# Revit family: RN 85142 Optiflex-Profix-Té
name_source: partatom
category: Rohrformteile
units: mm (PartAtom-declared; Revit-internal decimal feet)

## family parameters
Arbeitsebenenbasiert = Nein
Beim Laden mit Abzugskörper schneiden = Nein
Bemaßung runder Anschluss = Durchmesser verwenden
Gemeinsam genutzt = Nein
Immer vertikal = Ja
Teiletyp = T-Stück

## types (11) — shared parameters
1.010.00.2 Blattnummer der Richtlinie = 29
1.010.00.3 Ausgabedatum (Monat) der Richtlinie = 201308
1.010.00.4 Herstellername = R. Nussbaum AG
1.010.00.5 Revisionsdatum der Datei = 20190521
1.010.00.6 Webadresse des Herstellers = http://www.nussbaum.ch
1.100.00.4 Produktbezeichnung = Versorgung
1.110.00.2 Index = 5
1.110.00.4 Produktbezeichnung = Optiflex
1.960/3L.00.8 Link (URL) = https://www.nussbaum.ch
29.700.00.4 Produktname = Optiflex-Profix-T-Stück
29.700.00.5 Produktkennung = 2
29.700.00.6 Querschnittsform = 1
29.700.00.7 Nennweitensystem = DN
29.700.00.8 Nenndrucksystem = PN
29.710.02.4 Nenndruck = 10
29.710.02.5 max. zul. Überdruck [hPa] = 1000
29.710.02.7 max. zul. Dauer-Betriebsdruck [hPa] = 1000
29.710.02.9 max. zul. Dauer-Betriebstemperatur [°C] = 70
Connector Visibility = Nein
EnclosingSpace Visibility = Nein
Hersteller = R. Nussbaum AG
R. Nussbaum AG 85142.25 de Visibility = Nein
R. Nussbaum AG 85142.29 de Visibility = Nein
R. Nussbaum AG 85142.30 de Visibility = Nein
URL = https://www.nussbaum.ch

## per-type parameters (varying)
- DN=20x15x20: 1.800.00.3 TGA-Nummer=01900500000000000000000000000000000000000000000056000000000000000008; 1.800.00.4 Kommentarfeld=85142.28, Optiflex-Profix-T-Stück, DN=20x15x20, L=128; 1.810.00.3 Hersteller-Bestellnummer=85142.28; 1.810.00.4 DATANORM-Nummer=85142.28; 1.810.00.5 StLB-Nummer=331.633; 1.810.00.6 GTIN-Nummer=7612945698001; 29.710.02.10 Formstück-Gewicht [kg]=0.363; 29.710.02.3 Benennung=Optiflex-Profix-T-Stück, DN=20x15x20, L=128; CONNECTOR0_DIAMETER_dY_0r=20 mm; CONNECTOR0_dY_00=22 mm; CONNECTOR0_dY_01=64 mm; CONNECTOR0_ref_dY=22 mm; CONNECTOR1_DIAMETER_dY_0r=20 mm; CONNECTOR1_dY_00=64 mm; CONNECTOR1_dY_01=22 mm; CONNECTOR1_ref_dY=22 mm; CONNECTOR2_DIAMETER_dX_0r=12 mm  [stored 0.0393701 ft]; CONNECTOR2_dX_00=56 mm; CONNECTOR2_dX_01=22 mm; CONNECTOR2_ref_dX=22 mm; Modell=85142.28; R. Nussbaum AG 85142.21 de Visibility=Nein; R. Nussbaum AG 85142.22 de Visibility=Nein; R. Nussbaum AG 85142.23 de Visibility=Nein; R. Nussbaum AG 85142.24 de Visibility=Nein; R. Nussbaum AG 85142.26 de Visibility=Nein; R. Nussbaum AG 85142.27 de Visibility=Nein; R. Nussbaum AG 85142.28 de Visibility=Ja; R. Nussbaum AG 85142.31 de Visibility=Nein; Typenkommentare=Optiflex-Profix-Té  DN=20x15x20
- DN=25: 1.800.00.3 TGA-Nummer=01900500000000000000000000000000000000000000000056000000000000000010; 1.800.00.4 Kommentarfeld=85142.31, Optiflex-Profix-T-Stück, DN=25, L=128; 1.810.00.3 Hersteller-Bestellnummer=85142.31; 1.810.00.4 DATANORM-Nummer=85142.31; 1.810.00.5 StLB-Nummer=331.633; 1.810.00.6 GTIN-Nummer=7612945698032; 29.710.02.10 Formstück-Gewicht [kg]=0.43; 29.710.02.3 Benennung=Optiflex-Profix-T-Stück, DN=25, L=128; CONNECTOR0_DIAMETER_dY_0r=20 mm; CONNECTOR0_dY_00=22 mm; CONNECTOR0_dY_01=64 mm; CONNECTOR0_ref_dY=22 mm; CONNECTOR1_DIAMETER_dY_0r=20 mm; CONNECTOR1_dY_00=64 mm; CONNECTOR1_dY_01=22 mm; CONNECTOR1_ref_dY=22 mm; CONNECTOR2_DIAMETER_dX_0r=20 mm; CONNECTOR2_dX_00=64 mm; CONNECTOR2_dX_01=22 mm; CONNECTOR2_ref_dX=22 mm; Modell=85142.31; R. Nussbaum AG 85142.21 de Visibility=Nein; R. Nussbaum AG 85142.22 de Visibility=Nein; R. Nussbaum AG 85142.23 de Visibility=Nein; R. Nussbaum AG 85142.24 de Visibility=Nein; R. Nussbaum AG 85142.26 de Visibility=Nein; R. Nussbaum AG 85142.27 de Visibility=Nein; R. Nussbaum AG 85142.28 de Visibility=Nein; R. Nussbaum AG 85142.31 de Visibility=Ja; Typenkommentare=Optiflex-Profix-Té  DN=25
- DN=20x15x15: 1.800.00.3 TGA-Nummer=01900500000000000000000000000000000000000000000056000000000000000007; 1.800.00.4 Kommentarfeld=85142.27, Optiflex-Profix-T-Stück, DN=20x15x15, L=120; 1.810.00.3 Hersteller-Bestellnummer=85142.27; 1.810.00.4 DATANORM-Nummer=85142.27; 1.810.00.5 StLB-Nummer=331.633; 1.810.00.6 GTIN-Nummer=7612945697998; 29.710.02.10 Formstück-Gewicht [kg]=0.299; 29.710.02.3 Benennung=Optiflex-Profix-T-Stück, DN=20x15x15, L=120; CONNECTOR0_DIAMETER_dY_0r=20 mm; CONNECTOR0_dY_00=22 mm; CONNECTOR0_dY_01=64 mm; CONNECTOR0_ref_dY=22 mm; CONNECTOR1_DIAMETER_dY_0r=15 mm; CONNECTOR1_dY_00=56 mm; CONNECTOR1_dY_01=22 mm; CONNECTOR1_ref_dY=22 mm; CONNECTOR2_DIAMETER_dX_0r=12 mm  [stored 0.0393701 ft]; CONNECTOR2_dX_00=56 mm; CONNECTOR2_dX_01=22 mm; CONNECTOR2_ref_dX=22 mm; Modell=85142.27; R. Nussbaum AG 85142.21 de Visibility=Nein; R. Nussbaum AG 85142.22 de Visibility=Nein; R. Nussbaum AG 85142.23 de Visibility=Nein; R. Nussbaum AG 85142.24 de Visibility=Nein; R. Nussbaum AG 85142.26 de Visibility=Nein; R. Nussbaum AG 85142.27 de Visibility=Ja; R. Nussbaum AG 85142.28 de Visibility=Nein; R. Nussbaum AG 85142.31 de Visibility=Nein; Typenkommentare=Optiflex-Profix-Té  DN=20x15x15
- DN=15: 1.800.00.3 TGA-Nummer=01900500000000000000000000000000000000000000000056000000000000000006; 1.800.00.4 Kommentarfeld=85142.26, Optiflex-Profix-T-Stück, DN=15, L=108; 1.810.00.3 Hersteller-Bestellnummer=85142.26; 1.810.00.4 DATANORM-Nummer=85142.26; 1.810.00.5 StLB-Nummer=331.612; 1.810.00.6 GTIN-Nummer=7612945686701; 29.710.02.10 Formstück-Gewicht [kg]=0.235; 29.710.02.3 Benennung=Optiflex-Profix-T-Stück, DN=15, L=108; CONNECTOR0_DIAMETER_dY_0r=15 mm; CONNECTOR0_dY_00=20 mm; CONNECTOR0_dY_01=54 mm; CONNECTOR0_ref_dY=20 mm; CONNECTOR1_DIAMETER_dY_0r=15 mm; CONNECTOR1_dY_00=54 mm; CONNECTOR1_dY_01=20 mm; CONNECTOR1_ref_dY=20 mm; CONNECTOR2_DIAMETER_dX_0r=15 mm; CONNECTOR2_dX_00=54 mm; CONNECTOR2_dX_01=20 mm; CONNECTOR2_ref_dX=20 mm; Modell=85142.26; R. Nussbaum AG 85142.21 de Visibility=Nein; R. Nussbaum AG 85142.22 de Visibility=Nein; R. Nussbaum AG 85142.23 de Visibility=Nein; R. Nussbaum AG 85142.24 de Visibility=Nein; R. Nussbaum AG 85142.26 de Visibility=Ja; R. Nussbaum AG 85142.27 de Visibility=Nein; R. Nussbaum AG 85142.28 de Visibility=Nein; R. Nussbaum AG 85142.31 de Visibility=Nein; Typenkommentare=Optiflex-Profix-Té  DN=15
- DN=15x12x12: 1.800.00.3 TGA-Nummer=01900500000000000000000000000000000000000000000056000000000000000003; 1.800.00.4 Kommentarfeld=85142.23, Optiflex-Profix-T-Stück, DN=15x12x12, L=106; 1.810.00.3 Hersteller-Bestellnummer=85142.23; 1.810.00.4 DATANORM-Nummer=85142.23; 1.810.00.5 StLB-Nummer=331.632; 1.810.00.6 GTIN-Nummer=7612945686671; 29.710.02.10 Formstück-Gewicht [kg]=0.211; 29.710.02.3 Benennung=Optiflex-Profix-T-Stück, DN=15x12x12, L=106; CONNECTOR0_DIAMETER_dY_0r=15 mm; CONNECTOR0_dY_00=20 mm; CONNECTOR0_dY_01=54 mm; CONNECTOR0_ref_dY=20 mm; CONNECTOR1_DIAMETER_dY_0r=12 mm  [stored 0.0393701 ft]; CONNECTOR1_dY_00=52 mm; CONNECTOR1_dY_01=18 mm; CONNECTOR1_ref_dY=18 mm; CONNECTOR2_DIAMETER_dX_0r=12 mm  [stored 0.0393701 ft]; CONNECTOR2_dX_00=52 mm; CONNECTOR2_dX_01=18 mm; CONNECTOR2_ref_dX=18 mm; Modell=85142.23; R. Nussbaum AG 85142.21 de Visibility=Nein; R. Nussbaum AG 85142.22 de Visibility=Nein; R. Nussbaum AG 85142.23 de Visibility=Ja; R. Nussbaum AG 85142.24 de Visibility=Nein; R. Nussbaum AG 85142.26 de Visibility=Nein; R. Nussbaum AG 85142.27 de Visibility=Nein; R. Nussbaum AG 85142.28 de Visibility=Nein; R. Nussbaum AG 85142.31 de Visibility=Nein; Typenkommentare=Optiflex-Profix-Té  DN=15x12x12
- DN=15x12x15: 1.800.00.3 TGA-Nummer=01900500000000000000000000000000000000000000000056000000000000000004; 1.800.00.4 Kommentarfeld=85142.24, Optiflex-Profix-T-Stück, DN=15x12x15, L=108; 1.810.00.3 Hersteller-Bestellnummer=85142.24; 1.810.00.4 DATANORM-Nummer=85142.24; 1.810.00.5 StLB-Nummer=331.632; 1.810.00.6 GTIN-Nummer=7612945686688; 29.710.02.10 Formstück-Gewicht [kg]=0.223; 29.710.02.3 Benennung=Optiflex-Profix-T-Stück, DN=15x12x15, L=108; CONNECTOR0_DIAMETER_dY_0r=15 mm; CONNECTOR0_dY_00=20 mm; CONNECTOR0_dY_01=54 mm; CONNECTOR0_ref_dY=20 mm; CONNECTOR1_DIAMETER_dY_0r=15 mm; CONNECTOR1_dY_00=54 mm; CONNECTOR1_dY_01=20 mm; CONNECTOR1_ref_dY=20 mm; CONNECTOR2_DIAMETER_dX_0r=12 mm  [stored 0.0393701 ft]; CONNECTOR2_dX_00=52 mm; CONNECTOR2_dX_01=18 mm; CONNECTOR2_ref_dX=18 mm; Modell=85142.24; R. Nussbaum AG 85142.21 de Visibility=Nein; R. Nussbaum AG 85142.22 de Visibility=Nein; R. Nussbaum AG 85142.23 de Visibility=Nein; R. Nussbaum AG 85142.24 de Visibility=Ja; R. Nussbaum AG 85142.26 de Visibility=Nein; R. Nussbaum AG 85142.27 de Visibility=Nein; R. Nussbaum AG 85142.28 de Visibility=Nein; R. Nussbaum AG 85142.31 de Visibility=Nein; Typenkommentare=Optiflex-Profix-Té  DN=15x12x15
- DN=12x15x12: 1.800.00.3 TGA-Nummer=01900500000000000000000000000000000000000000000056000000000000000002; 1.800.00.4 Kommentarfeld=85142.22, Optiflex-Profix-T-Stück, DN=12x15x12, L=104; 1.810.00.3 Hersteller-Bestellnummer=85142.22; 1.810.00.4 DATANORM-Nummer=85142.22; 1.810.00.5 StLB-Nummer=331.632; 1.810.00.6 GTIN-Nummer=7612945686664; 29.710.02.10 Formstück-Gewicht [kg]=0.213; 29.710.02.3 Benennung=Optiflex-Profix-T-Stück, DN=12x15x12, L=104; CONNECTOR0_DIAMETER_dY_0r=12 mm  [stored 0.0393701 ft]; CONNECTOR0_dY_00=18 mm; CONNECTOR0_dY_01=52 mm; CONNECTOR0_ref_dY=18 mm; CONNECTOR1_DIAMETER_dY_0r=12 mm  [stored 0.0393701 ft]; CONNECTOR1_dY_00=52 mm; CONNECTOR1_dY_01=18 mm; CONNECTOR1_ref_dY=18 mm; CONNECTOR2_DIAMETER_dX_0r=15 mm; CONNECTOR2_dX_00=54 mm; CONNECTOR2_dX_01=20 mm; CONNECTOR2_ref_dX=20 mm; Modell=85142.22; R. Nussbaum AG 85142.21 de Visibility=Nein; R. Nussbaum AG 85142.22 de Visibility=Ja; R. Nussbaum AG 85142.23 de Visibility=Nein; R. Nussbaum AG 85142.24 de Visibility=Nein; R. Nussbaum AG 85142.26 de Visibility=Nein; R. Nussbaum AG 85142.27 de Visibility=Nein; R. Nussbaum AG 85142.28 de Visibility=Nein; R. Nussbaum AG 85142.31 de Visibility=Nein; Typenkommentare=Optiflex-Profix-Té  DN=12x15x12
- DN=12: 1.800.00.3 TGA-Nummer=01900500000000000000000000000000000000000000000056000000000000000001; 1.800.00.4 Kommentarfeld=85142.21, Optiflex-Profix-T-Stück, DN=12, L=104; 1.810.00.3 Hersteller-Bestellnummer=85142.21; 1.810.00.4 DATANORM-Nummer=85142.21; 1.810.00.5 StLB-Nummer=331.611; 1.810.00.6 GTIN-Nummer=7612945686657; 29.710.02.10 Formstück-Gewicht [kg]=0.192; 29.710.02.3 Benennung=Optiflex-Profix-T-Stück, DN=12, L=104; CONNECTOR0_DIAMETER_dY_0r=12 mm  [stored 0.0393701 ft]; CONNECTOR0_dY_00=18 mm; CONNECTOR0_dY_01=52 mm; CONNECTOR0_ref_dY=18 mm; CONNECTOR1_DIAMETER_dY_0r=12 mm  [stored 0.0393701 ft]; CONNECTOR1_dY_00=52 mm; CONNECTOR1_dY_01=18 mm; CONNECTOR1_ref_dY=18 mm; CONNECTOR2_DIAMETER_dX_0r=12 mm  [stored 0.0393701 ft]; CONNECTOR2_dX_00=52 mm; CONNECTOR2_dX_01=18 mm; CONNECTOR2_ref_dX=18 mm; Modell=85142.21; R. Nussbaum AG 85142.21 de Visibility=Ja; R. Nussbaum AG 85142.22 de Visibility=Nein; R. Nussbaum AG 85142.23 de Visibility=Nein; R. Nussbaum AG 85142.24 de Visibility=Nein; R. Nussbaum AG 85142.26 de Visibility=Nein; R. Nussbaum AG 85142.27 de Visibility=Nein; R. Nussbaum AG 85142.28 de Visibility=Nein; R. Nussbaum AG 85142.31 de Visibility=Nein; Typenkommentare=Optiflex-Profix-Té  DN=12
- DN=20x15x2: 1.800.00.3 TGA-Nummer=01900500000000000000000000000000000000000000000056000000000000000007; 1.800.00.4 Kommentarfeld=85142.27, Optiflex-Profix-T-Stück, DN=20x15x15, L=120; 1.810.00.3 Hersteller-Bestellnummer=85142.27; 1.810.00.4 DATANORM-Nummer=85142.27; 1.810.00.5 StLB-Nummer=331.633; 1.810.00.6 GTIN-Nummer=7612945697998; 29.710.02.10 Formstück-Gewicht [kg]=0.299; 29.710.02.3 Benennung=Optiflex-Profix-T-Stück, DN=20x15x15, L=120; CONNECTOR0_DIAMETER_dY_0r=20 mm; CONNECTOR0_dY_00=22 mm; CONNECTOR0_dY_01=64 mm; CONNECTOR0_ref_dY=22 mm; CONNECTOR1_DIAMETER_dY_0r=15 mm; CONNECTOR1_dY_00=56 mm; CONNECTOR1_dY_01=22 mm; CONNECTOR1_ref_dY=22 mm; CONNECTOR2_DIAMETER_dX_0r=12 mm  [stored 0.0393701 ft]; CONNECTOR2_dX_00=56 mm; CONNECTOR2_dX_01=22 mm; CONNECTOR2_ref_dX=22 mm; Modell=85142.27; R. Nussbaum AG 85142.21 de Visibility=Nein; R. Nussbaum AG 85142.22 de Visibility=Nein; R. Nussbaum AG 85142.23 de Visibility=Nein; R. Nussbaum AG 85142.24 de Visibility=Nein; R. Nussbaum AG 85142.26 de Visibility=Nein; R. Nussbaum AG 85142.27 de Visibility=Ja; R. Nussbaum AG 85142.28 de Visibility=Nein; R. Nussbaum AG 85142.31 de Visibility=Nein; Typenkommentare=Optiflex-Profix-Té  DN=20x15x15
- DN=20x15x1: 1.800.00.3 TGA-Nummer=01900500000000000000000000000000000000000000000056000000000000000008; 1.800.00.4 Kommentarfeld=85142.28, Optiflex-Profix-T-Stück, DN=20x15x20, L=128; 1.810.00.3 Hersteller-Bestellnummer=85142.28; 1.810.00.4 DATANORM-Nummer=85142.28; 1.810.00.5 StLB-Nummer=331.633; 1.810.00.6 GTIN-Nummer=7612945698001; 29.710.02.10 Formstück-Gewicht [kg]=0.363; 29.710.02.3 Benennung=Optiflex-Profix-T-Stück, DN=20x15x20, L=128; CONNECTOR0_DIAMETER_dY_0r=20 mm; CONNECTOR0_dY_00=22 mm; CONNECTOR0_dY_01=64 mm; CONNECTOR0_ref_dY=22 mm; CONNECTOR1_DIAMETER_dY_0r=20 mm; CONNECTOR1_dY_00=64 mm; CONNECTOR1_dY_01=22 mm; CONNECTOR1_ref_dY=22 mm; CONNECTOR2_DIAMETER_dX_0r=12 mm  [stored 0.0393701 ft]; CONNECTOR2_dX_00=56 mm; CONNECTOR2_dX_01=22 mm; CONNECTOR2_ref_dX=22 mm; Modell=85142.28; R. Nussbaum AG 85142.21 de Visibility=Nein; R. Nussbaum AG 85142.22 de Visibility=Nein; R. Nussbaum AG 85142.23 de Visibility=Nein; R. Nussbaum AG 85142.24 de Visibility=Nein; R. Nussbaum AG 85142.26 de Visibility=Nein; R. Nussbaum AG 85142.27 de Visibility=Nein; R. Nussbaum AG 85142.28 de Visibility=Ja; R. Nussbaum AG 85142.31 de Visibility=Nein; Typenkommentare=Optiflex-Profix-Té  DN=20x15x20
- DN=15x12x1: 1.800.00.3 TGA-Nummer=01900500000000000000000000000000000000000000000056000000000000000003; 1.800.00.4 Kommentarfeld=85142.23, Optiflex-Profix-T-Stück, DN=15x12x12, L=106; 1.810.00.3 Hersteller-Bestellnummer=85142.23; 1.810.00.4 DATANORM-Nummer=85142.23; 1.810.00.5 StLB-Nummer=331.632; 1.810.00.6 GTIN-Nummer=7612945686671; 29.710.02.10 Formstück-Gewicht [kg]=0.211; 29.710.02.3 Benennung=Optiflex-Profix-T-Stück, DN=15x12x12, L=106; CONNECTOR0_DIAMETER_dY_0r=15 mm; CONNECTOR0_dY_00=20 mm; CONNECTOR0_dY_01=54 mm; CONNECTOR0_ref_dY=20 mm; CONNECTOR1_DIAMETER_dY_0r=12 mm  [stored 0.0393701 ft]; CONNECTOR1_dY_00=52 mm; CONNECTOR1_dY_01=18 mm; CONNECTOR1_ref_dY=18 mm; CONNECTOR2_DIAMETER_dX_0r=12 mm  [stored 0.0393701 ft]; CONNECTOR2_dX_00=52 mm; CONNECTOR2_dX_01=18 mm; CONNECTOR2_ref_dX=18 mm; Modell=85142.23; R. Nussbaum AG 85142.21 de Visibility=Nein; R. Nussbaum AG 85142.22 de Visibility=Nein; R. Nussbaum AG 85142.23 de Visibility=Ja; R. Nussbaum AG 85142.24 de Visibility=Nein; R. Nussbaum AG 85142.26 de Visibility=Nein; R. Nussbaum AG 85142.27 de Visibility=Nein; R. Nussbaum AG 85142.28 de Visibility=Nein; R. Nussbaum AG 85142.31 de Visibility=Nein; Typenkommentare=Optiflex-Profix-Té  DN=15x12x12

note: [stored X ft] marks values corroborated as IEEE doubles in the binary element streams (Revit-internal decimal feet)

## geometry (parser evidence)
native form markers: Sweep x2
no freeform markers — native parametric forms only
